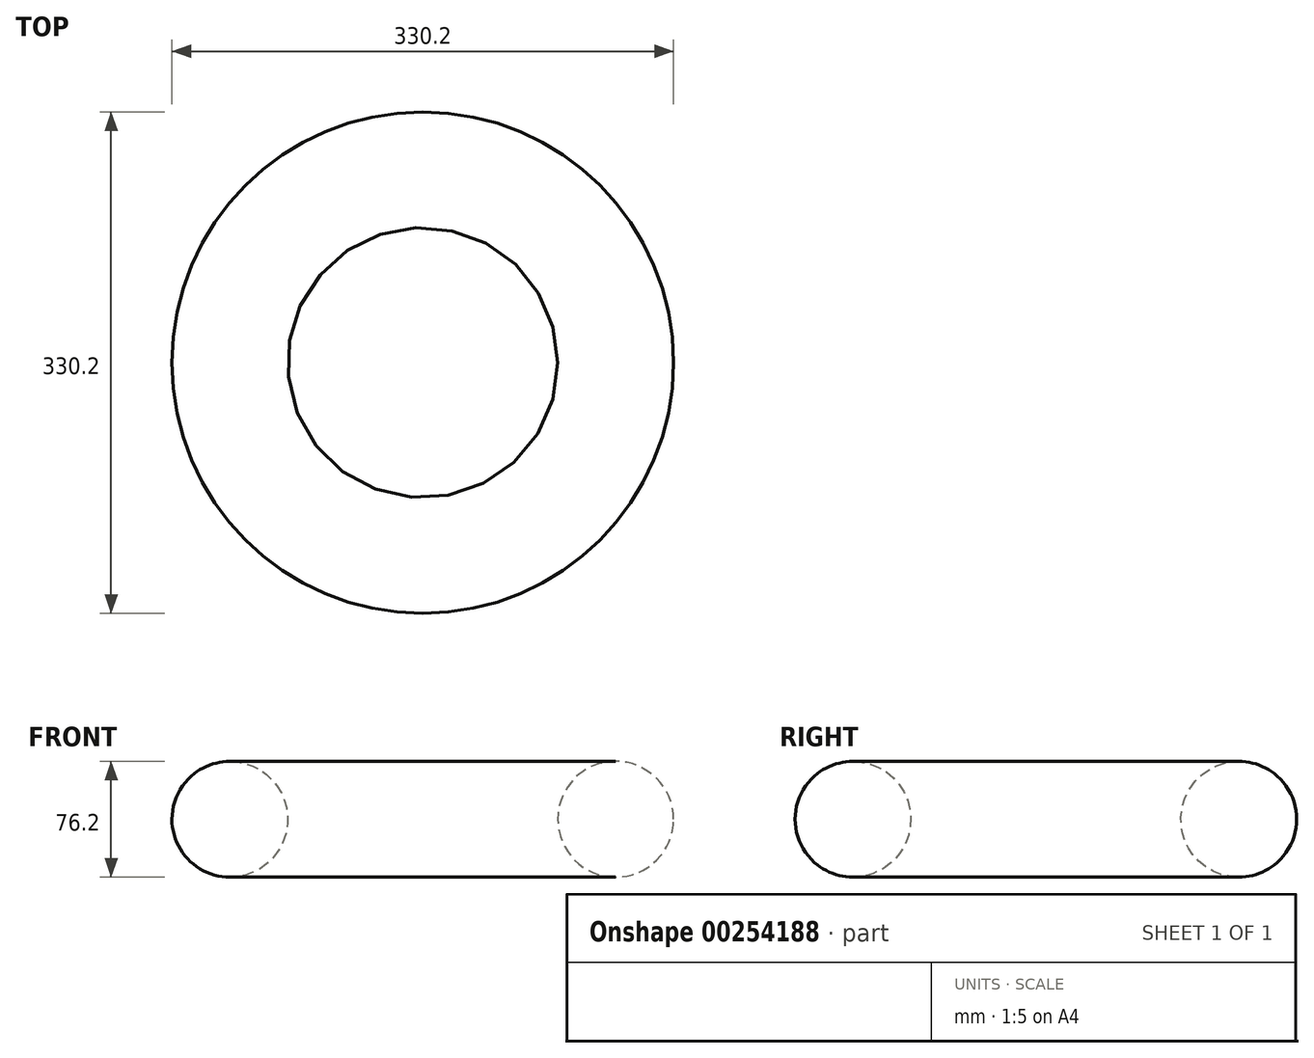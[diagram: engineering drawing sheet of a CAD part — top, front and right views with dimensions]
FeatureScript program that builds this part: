
annotation { "Feature Type Name" : "Feature", "Feature Type Description" : "" }
export const myFeature = defineFeature(function(context is Context, id is Id, definition is map)
    precondition{}
    {
        {
            var Q0;
            Q0=qCreatedBy(makeId("Front.planeOp"),FACE);
            var sketch = newSketch(context, id + "F0", { "sketchPlane" : qUnion([Q0])});
            skCircle(sketch, "E0", {"center": v(-127, 25.87) * mm, "radius": 38.1 * mm});
            skSolve(sketch);
        }
        {
            var Q0;
            Q0=qCreatedBy(makeId("Front.planeOp"),FACE);
            var sketch = newSketch(context, id + "F1", { "sketchPlane" : qUnion([Q0])});
            skLineSegment(sketch, "E1", {"start": v(0, 75.2) * mm, "end": v(0, -75.2) * mm, "construction": true});
            skSolve(sketch);
        }
        {
            var Q0;
            Q0=makeQuery(id+"F0.imprint","IMPRINT",FACE,{"disambiguationData":[TD([[makeQuery(id+"F0.imprint","IMPRINT",EDGE,{"derivedFrom":sQuery(id+"F0.wireOp",EDGE,"E0")}),1.0]])]});
            var Q1;
            Q1=sQuery(id+"F1.wireOp",EDGE,"E1");
            revolve(context, id + "F2", {"entities" : qUnion([Q0]), "axis" : qUnion([Q1]), "revolveType" : RevolveType.FULL});
        }
    });
